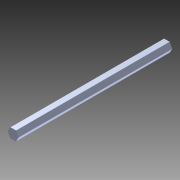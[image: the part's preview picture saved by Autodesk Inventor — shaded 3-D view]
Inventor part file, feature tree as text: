
AUTODESK INVENTOR PART (.ipt)
format: ipt  version: 2014 (Build 180170000, 170)  size: 118,784 bytes
history: native  units: in
note: dims shown in document units (in); Inventor stores cm internally (conversion verified against a paired STEP export)
features: fillet x1, other x1, extrude x1, imported_body x1, sketch x1
ambient origin geometry x8: Origin, YZ Plane, XZ Plane, XY Plane, X Axis, Y Axis, Z Axis, Center Point
bodies: Body1 (feature_tree)
feature tree (5):
  fillet  "Fillet1"  Radius=10.0in
  other  "18inShaft1"
  extrude  "Extrusion1"  [1 undecoded]
  imported_body  "Base1"
  sketch  "Sketch1"
note: 1 required parameter value undecoded (feature->parameter linkage not recoverable at this tier; creation-order binding heuristic only, values carry confidence <= 0.55)
